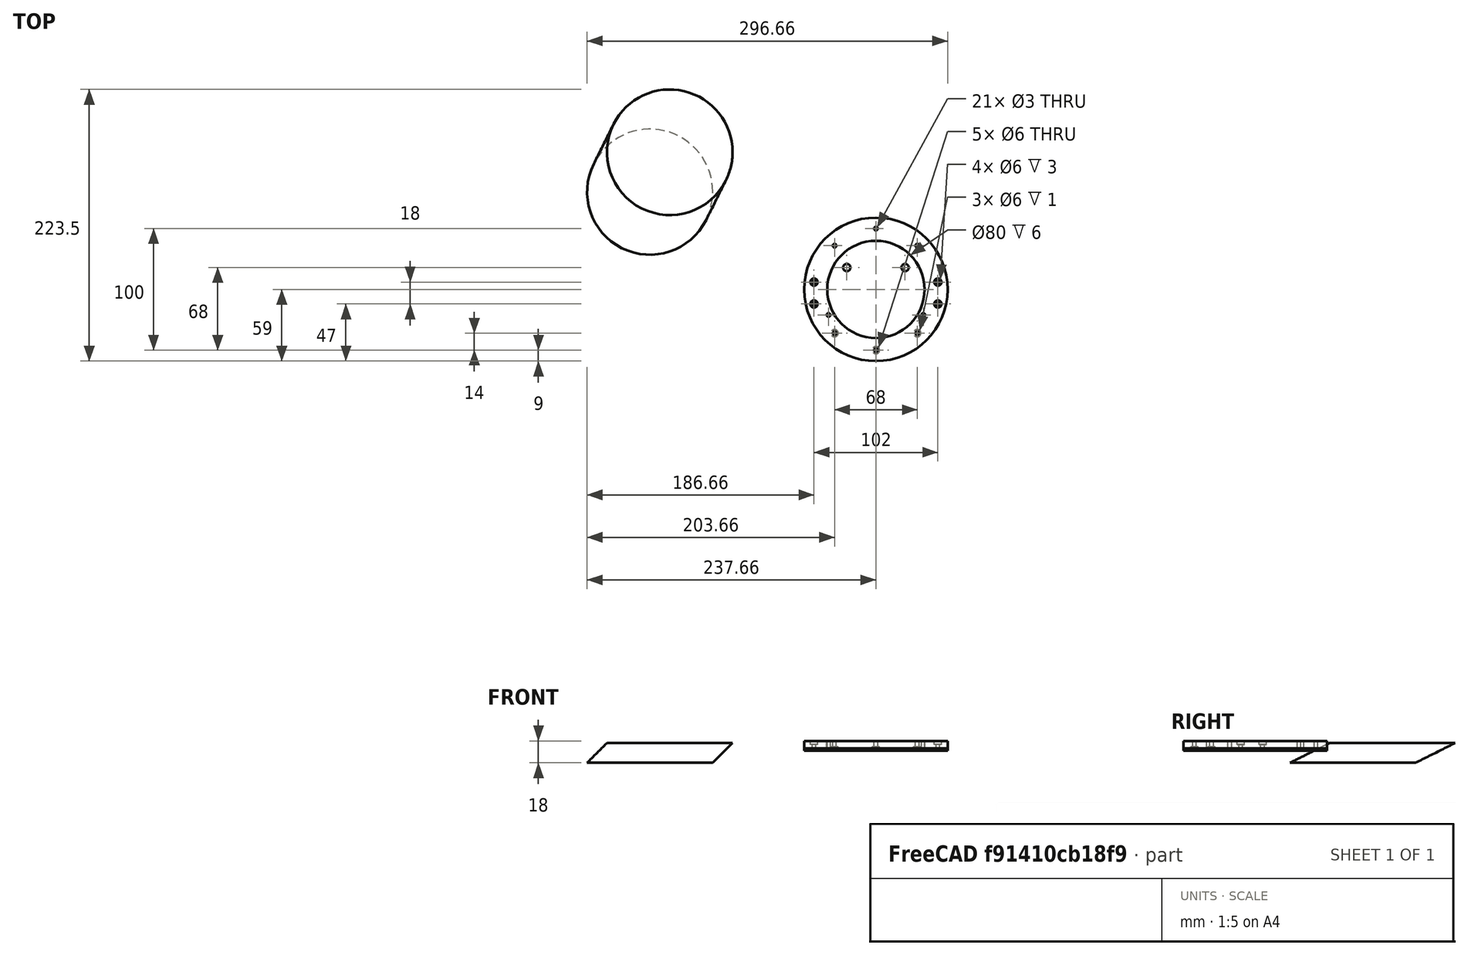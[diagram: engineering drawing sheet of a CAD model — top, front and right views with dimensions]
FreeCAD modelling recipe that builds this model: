
FCSTD DOCUMENT  (FreeCAD 0.19R24276 (Git))
Label: bazovina-part-B_vicko_007
License: All rights reserved
LicenseURL: http://en.wikipedia.org/wiki/All_rights_reserved
objects: Part::Cylinder×36, Part::Cut×16, Part::Compound×12, Part::FeaturePython×1, Sketcher::SketchObject×1, Part::Extrusion×1, Mesh::Feature×1
note: 67 computed .brp shape members not serialized (recipe doc carries the construction recipe); baked Part::Feature solids carry a one-line shape summary decoded from their .brp

FEATURE [Part::FeaturePython] Tube018  # WARN: FeaturePython — macro-defined, semantics opaque (R4)
  AttacherType = Attacher::AttachEngine3D
  Height = 6
  InnerRadius = 40
  OuterRadius = 59
  Placement = pos=(0,0,12) rot=(0,0,1;0rad)
FEATURE [Part::Cylinder] Cylinder302  label="Válec302"
  Angle = 360
  AttacherType = Attacher::AttachEngine3D
  Height = 50
  Placement = pos=(-34,36,0) rot=(0,0,1;0rad)
  Radius = 1.5
FEATURE [Part::Cylinder] Cylinder287  label="Válec287"
  Angle = 360
  AttacherType = Attacher::AttachEngine3D
  Height = 2
  Placement = pos=(0,0,10) rot=(0,0,1;0rad)
  Radius = 59
FEATURE [Part::Cylinder] Cylinder301  label="Válec301"
  Angle = 360
  AttacherType = Attacher::AttachEngine3D
  Height = 50
  Placement = pos=(34,36,0) rot=(0,0,1;0rad)
  Radius = 1.5
FEATURE [Part::Compound] Compound285
  Links = -> [Cylinder302,Cylinder301]
FEATURE [Part::Cut] Cut133
  Base = -> Tube018
  Tool = -> Compound285
FEATURE [Part::Cylinder] Cylinder337  label="Válec337"
  Angle = 360
  AttacherType = Attacher::AttachEngine3D
  Height = 100
  Placement = pos=(-51,-12,0) rot=(0,0,1;0rad)
  Radius = 1.5
FEATURE [Part::Cylinder] Cylinder338  label="Válec338"
  Angle = 360
  AttacherType = Attacher::AttachEngine3D
  Height = 100
  Placement = pos=(51,-12,0) rot=(0,0,1;0rad)
  Radius = 1.5
FEATURE [Part::Cylinder] Cylinder340  label="Válec340"
  Angle = 360
  AttacherType = Attacher::AttachEngine3D
  Height = 50
  Placement = pos=(51,6,0) rot=(0,0,1;0rad)
  Radius = 1.5
FEATURE [Part::Cylinder] Cylinder333  label="Válec333"
  Angle = 360
  AttacherType = Attacher::AttachEngine3D
  Height = 4
  Placement = pos=(51,6,17) rot=(0,0,1;0rad)
  Radius = 3
FEATURE [Part::Cylinder] Cylinder343  label="Válec343"
  Angle = 360
  AttacherType = Attacher::AttachEngine3D
  Height = 50
  Placement = pos=(34,36,0) rot=(0,0,1;0rad)
  Radius = 1.5
FEATURE [Part::Cylinder] Cylinder344  label="Válec344"
  Angle = 360
  AttacherType = Attacher::AttachEngine3D
  Height = 50
  Placement = pos=(-34,36,0) rot=(0,0,1;0rad)
  Radius = 1.5
FEATURE [Part::Cylinder] Cylinder345  label="Válec345"
  Angle = 360
  AttacherType = Attacher::AttachEngine3D
  Height = 100
  Placement = pos=(-51,-12,0) rot=(0,0,1;0rad)
  Radius = 1.5
FEATURE [Part::Cylinder] Cylinder332  label="Válec332"
  Angle = 360
  AttacherType = Attacher::AttachEngine3D
  Height = 4
  Placement = pos=(-51,6,17) rot=(0,0,1;0rad)
  Radius = 3
FEATURE [Part::Compound] Compound300
  Links = -> [Cylinder333,Cylinder332]
  Placement = pos=(0,0,-2) rot=(0,0,1;0rad)
FEATURE [Part::Cylinder] Cylinder339  label="Válec339"
  Angle = 360
  AttacherType = Attacher::AttachEngine3D
  Height = 50
  Placement = pos=(-51,6,0) rot=(0,0,1;0rad)
  Radius = 1.5
FEATURE [Part::Compound] Compound301
  Links = -> [Cylinder337,Cylinder344,Cylinder343,Cylinder340,Cylinder339,Cylinder338]
FEATURE [Part::Cylinder] Cylinder346  label="Válec346"
  Angle = 360
  AttacherType = Attacher::AttachEngine3D
  Height = 100
  Placement = pos=(51,-12,0) rot=(0,0,1;0rad)
  Radius = 1.5
FEATURE [Part::Cylinder] Cylinder347  label="Válec347"
  Angle = 360
  AttacherType = Attacher::AttachEngine3D
  Height = 50
  Placement = pos=(51,6,0) rot=(0,0,1;0rad)
  Radius = 1.5
FEATURE [Part::Cut] Cut145
  Base = -> Cut133
  Tool = -> Compound301
FEATURE [Part::Cylinder] Cylinder352  label="Válec352"
  Angle = 360
  AttacherType = Attacher::AttachEngine3D
  Height = 4
  Placement = pos=(51,-12,0) rot=(0,0,1;0rad)
  Radius = 3
FEATURE [Part::Cylinder] Cylinder362  label="Válec362"
  Angle = 360
  AttacherType = Attacher::AttachEngine3D
  Height = 4
  Placement = pos=(34,-36,0) rot=(0,0,1;0rad)
  Radius = 3
FEATURE [Part::Cylinder] Cylinder365  label="Válec365"
  Angle = 360
  AttacherType = Attacher::AttachEngine3D
  Height = 50
  Placement = pos=(0,50,0) rot=(0,0,1;0rad)
  Radius = 1.5
FEATURE [Part::Cylinder] Cylinder350  label="Válec350"
  Angle = 360
  AttacherType = Attacher::AttachEngine3D
  Height = 50
  Placement = pos=(-34,36,0) rot=(0,0,1;0rad)
  Radius = 1.5
FEATURE [Part::Cylinder] Cylinder353  label="Válec353"
  Angle = 360
  AttacherType = Attacher::AttachEngine3D
  Height = 4
  Placement = pos=(-24,18,0) rot=(0,0,1;0rad)
  Radius = 3
FEATURE [Part::Cylinder] Cylinder358  label="Válec358"
  Angle = 360
  AttacherType = Attacher::AttachEngine3D
  Height = 50
  Placement = pos=(-34,-36,0) rot=(0,0,1;0rad)
  Radius = 1.5
FEATURE [Part::Cylinder] Cylinder356  label="Válec356"
  Angle = 360
  AttacherType = Attacher::AttachEngine3D
  Height = 4
  Placement = pos=(24,18,0) rot=(0,0,1;0rad)
  Radius = 3
FEATURE [Part::Compound] Compound304
  Links = -> [Cylinder353,Cylinder356]
  Placement = pos=(0,0,10) rot=(0,0,1;0rad)
FEATURE [Part::Cylinder] Cylinder348  label="Válec348"
  Angle = 360
  AttacherType = Attacher::AttachEngine3D
  Height = 50
  Placement = pos=(-51,6,0) rot=(0,0,1;0rad)
  Radius = 1.5
FEATURE [Part::Cylinder] Cylinder351  label="Válec351"
  Angle = 360
  AttacherType = Attacher::AttachEngine3D
  Height = 4
  Placement = pos=(-51,-12,0) rot=(0,0,1;0rad)
  Radius = 3
FEATURE [Part::Compound] Compound303
  Links = -> [Cylinder351,Cylinder352]
  Placement = pos=(0,0,15) rot=(0,0,1;0rad)
FEATURE [Part::Cut] Cut146
  Base = -> Cut145
  Tool = -> Compound303
FEATURE [Part::Cut] Cut147
  Base = -> Cut146
  Tool = -> Compound300
FEATURE [Part::Cylinder] Cylinder359  label="Válec359"
  Angle = 360
  AttacherType = Attacher::AttachEngine3D
  Height = 4
  Placement = pos=(34,-36,0) rot=(0,0,1;0rad)
  Radius = 3
FEATURE [Part::Cylinder] Cylinder360  label="Válec360"
  Angle = 360
  AttacherType = Attacher::AttachEngine3D
  Height = 4
  Placement = pos=(-34,-36,0) rot=(0,0,1;0rad)
  Radius = 3
FEATURE [Part::Compound] Compound305
  Links = -> [Cylinder359,Cylinder360]
  Placement = pos=(0,0,9) rot=(0,0,1;0rad)
FEATURE [Part::Cylinder] Cylinder361  label="Válec361"
  Angle = 360
  AttacherType = Attacher::AttachEngine3D
  Height = 4
  Placement = pos=(-34,-36,0) rot=(0,0,1;0rad)
  Radius = 3
FEATURE [Part::Compound] Compound307
  Links = -> [Cylinder362,Cylinder361]
  Placement = pos=(0,0,9) rot=(0,0,1;0rad)
FEATURE [Part::Cut] Cut151
  Base = -> Cut147
  Tool = -> Compound307
FEATURE [Part::Cylinder] Cylinder357  label="Válec357"
  Angle = 360
  AttacherType = Attacher::AttachEngine3D
  Height = 50
  Placement = pos=(34,-36,0) rot=(0,0,1;0rad)
  Radius = 1.5
FEATURE [Part::Compound] Compound306
  Links = -> [Cylinder357,Cylinder358]
FEATURE [Part::Cut] Cut152
  Base = -> Cut151
  Tool = -> Compound306
FEATURE [Part::Cylinder] Cylinder349  label="Válec349"
  Angle = 360
  AttacherType = Attacher::AttachEngine3D
  Height = 50
  Placement = pos=(34,36,0) rot=(0,0,1;0rad)
  Radius = 1.5
FEATURE [Part::Compound] Compound302
  Links = -> [Cylinder345,Cylinder350,Cylinder349,Cylinder347,Cylinder348,Cylinder346]
FEATURE [Part::Cut] Cut148
  Base = -> Cylinder287
  Tool = -> Compound302
FEATURE [Part::Cut] Cut149
  Base = -> Cut148
  Tool = -> Compound304
FEATURE [Part::Cut] Cut150
  Base = -> Cut149
  Tool = -> Compound305
FEATURE [Part::Cut] Cut155
  Base = -> Cut150
  Tool = -> Cylinder365
FEATURE [Part::Cylinder] Cylinder366  label="Válec366"
  Angle = 360
  AttacherType = Attacher::AttachEngine3D
  Height = 50
  Placement = pos=(0,50,0) rot=(0,0,1;0rad)
  Radius = 1.5
FEATURE [Part::Cut] Cut156
  Base = -> Cut152
  Tool = -> Cylinder366
FEATURE [Part::Cylinder] Cylinder367  label="Válec367"
  Angle = 360
  AttacherType = Attacher::AttachEngine3D
  Height = 4
  Placement = pos=(0,-50,9) rot=(0,0,1;0rad)
  Radius = 3
FEATURE [Part::Cut] Cut157
  Base = -> Cut155
  Tool = -> Cylinder367
FEATURE [Part::Cylinder] Cylinder369  label="Válec369"
  Angle = 360
  AttacherType = Attacher::AttachEngine3D
  Height = 4
  Placement = pos=(0,-50,9) rot=(0,0,1;0rad)
  Radius = 3
FEATURE [Part::Cut] Cut158
  Base = -> Cut156
  Tool = -> Cylinder369
FEATURE [Part::Cylinder] Cylinder368  label="Válec368"
  Angle = 360
  AttacherType = Attacher::AttachEngine3D
  Height = 50
  Placement = pos=(0,-50,0) rot=(0,0,1;0rad)
  Radius = 1.5
FEATURE [Part::Cut] Cut159
  Base = -> Cut158
  Tool = -> Cylinder368
FEATURE [Part::Cylinder] Cylinder528  label="Válec528"
  Angle = 360
  AttacherType = Attacher::AttachEngine3D
  Height = 100
  Placement = pos=(-39,-21,0) rot=(0,0,1;0rad)
  Radius = 1.5
FEATURE [Part::Cylinder] Cylinder529  label="Válec529"
  Angle = 360
  AttacherType = Attacher::AttachEngine3D
  Height = 100
  Placement = pos=(39,-21,0) rot=(0,0,1;0rad)
  Radius = 1.5
FEATURE [Part::Compound] Compound
  Links = -> [Cylinder528,Cylinder529]
FEATURE [Part::Cylinder] Cylinder530  label="Válec530"
  Angle = 360
  AttacherType = Attacher::AttachEngine3D
  Height = 100
  Placement = pos=(-39,-21,0) rot=(0,0,1;0rad)
  Radius = 1.5
FEATURE [Part::Cylinder] Cylinder531  label="Válec531"
  Angle = 360
  AttacherType = Attacher::AttachEngine3D
  Height = 100
  Placement = pos=(39,-21,0) rot=(0,0,1;0rad)
  Radius = 1.5
FEATURE [Part::Compound] Compound308
  Links = -> [Cylinder530,Cylinder531]
FEATURE [Part::Cut] Cut
  Base = -> Cut159
  Tool = -> Compound308
FEATURE [Part::Cut] Cut160
  Base = -> Cut157
  Tool = -> Compound
FEATURE [Part::Compound] Compound309  label="bazovina_part-B_vicko"
  Links = -> [Cut,Cut160]
FEATURE [Sketcher::SketchObject] Sketch
  FullyConstrained = false
  sketch-geometry (1):
    g0: Circle CenterX=-185.99 CenterY=80.1729 CenterZ=0 NormalX=0 NormalY=0 NormalZ=1 AngleXU=0 Radius=51.6665
FEATURE [Part::Extrusion] Extrude
  Base = -> Sketch
  Dir = (1,2,1)
  DirMode = 0
  FaceMakerClass = Part::FaceMakerBullseye
  LengthFwd = 40
  LengthRev = 0
  Solid = true
  Symmetric = false
FEATURE [Mesh::Feature] Mesh  label="Extrude (Meshed)"
